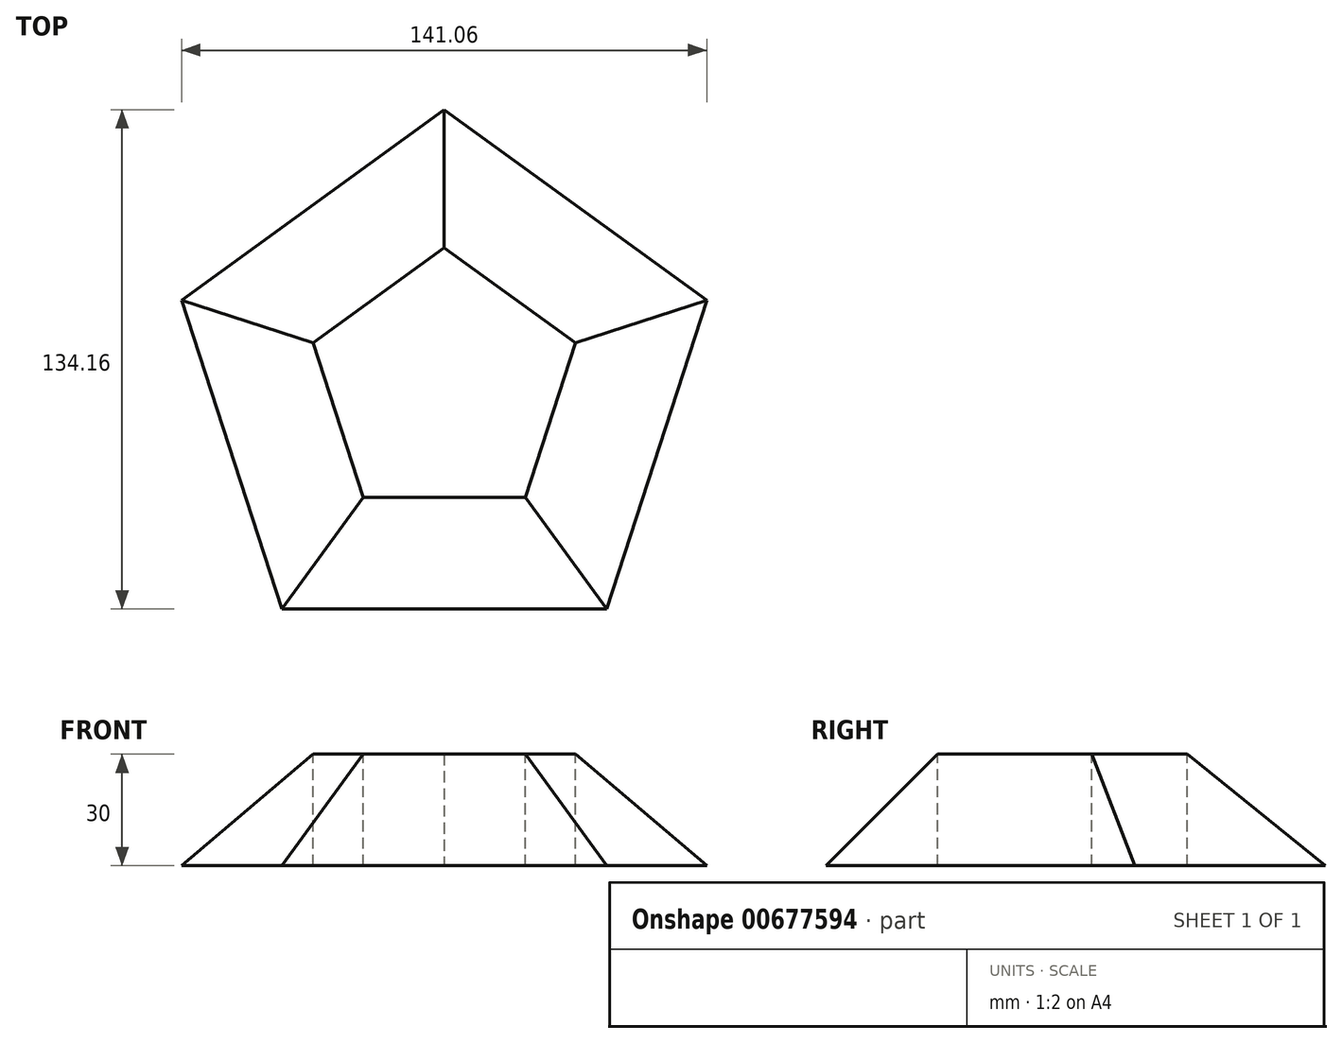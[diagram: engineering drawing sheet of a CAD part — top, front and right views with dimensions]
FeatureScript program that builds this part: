
annotation { "Feature Type Name" : "Feature", "Feature Type Description" : "" }
export const myFeature = defineFeature(function(context is Context, id is Id, definition is map)
    precondition{}
    {
        {
            var Q0;
            Q0=qCreatedBy(makeId("Top.planeOp"),FACE);
            var sketch = newSketch(context, id + "F0", { "sketchPlane" : qUnion([Q0])});
            skCircle(sketch, "E0.cCircle", {"center": v(0, 0) * mm, "radius": 74.16 * mm, "construction": true});
            skLineSegment(sketch, "E0.0", {"start": v(-70.53, 22.92) * mm, "end": v(0, 74.16) * mm});
            skLineSegment(sketch, "E0.1", {"start": v(0, 74.16) * mm, "end": v(70.53, 22.92) * mm});
            skLineSegment(sketch, "E0.2", {"start": v(70.53, 22.92) * mm, "end": v(43.6, -60) * mm});
            skLineSegment(sketch, "E0.3", {"start": v(43.6, -60) * mm, "end": v(-43.6, -60) * mm});
            skLineSegment(sketch, "E0.4", {"start": v(-43.6, -60) * mm, "end": v(-70.53, 22.92) * mm});
            skSolve(sketch);
        }
        {
            var Q0;
            Q0=makeQuery(id+"F0.imprint","IMPRINT",FACE,{"disambiguationData":[TD([[makeQuery(id+"F0.imprint","IMPRINT",EDGE,{"derivedFrom":sQuery(id+"F0.wireOp",EDGE,"E0.0")}),-1.0]])]});
            extrude(context, id + "F1", {"entities" : qUnion([Q0]), "depth" : 30 * mm, "offsetDistance" : 25 * mm, "hasDraft" : true, "draftAngle" : 45 * degree, "draftPullDirection" : true});
        }
        {
            var Q0;
            Q0=qCreatedBy(makeId("Top.planeOp"),FACE);
            cPlane(context, id + "F2", {"entities" : qUnion([Q0]), "cplaneType" : CPlaneType.OFFSET, "offset" : 30 * mm, "width" : 150 * mm, "height" : 150 * mm});
        }
        {
            var Q0;
            Q0=makeQuery(id+"F1.opExtrude","CAP_FACE",FACE,{"disambiguationData":[OSD([sQuery(id+"F0.wireOp",EDGE,"E0.0"),sQuery(id+"F0.wireOp",EDGE,"E0.1"),sQuery(id+"F0.wireOp",EDGE,"E0.2"),sQuery(id+"F0.wireOp",EDGE,"E0.3"),sQuery(id+"F0.wireOp",EDGE,"E0.4")])],"isStart":false});
            extrude(context, id + "F3", {"entities" : qUnion([Q0]), "operationType" : NewBodyOperationType.REMOVE, "oppositeDirection" : true, "depth" : 30 * mm, "offsetDistance" : 25 * mm});
        }
    });
